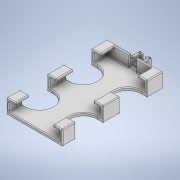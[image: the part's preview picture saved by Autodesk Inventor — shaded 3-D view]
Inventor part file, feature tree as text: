
AUTODESK INVENTOR PART (.ipt)
format: ipt  version: 2020.2 (Build 242310000, 310)  size: 641,536 bytes
history: native  units: in
note: dims shown in document units (in); Inventor stores cm internally (conversion verified against a paired STEP export)
features: sketch x7, extrude x6, fillet x5, hole x1
ambient origin geometry x8: Origin, YZ Plane, XZ Plane, XY Plane, X Axis, Y Axis, Z Axis, Center Point
bodies: Solid1 (feature_tree)
feature tree (19):
  extrude  "Extrusion1"  Depth=0.8in
  extrude  "Extrusion2"  Depth=0.5in
  extrude  "Extrusion3"  Depth=0.5in
  extrude  "Extrusion4"  Depth=0.8in
  hole  "Hole1"  [1 undecoded]
  sketch  "Sketch9"  dims[d12=0.15in d13=0.15in]
  extrude  "Extrusion5"  Depth=0.15in
  extrude  "Extrusion6"  Depth=0.3in
  fillet  "Fillet1"  Radius=0.3in
  fillet  "Fillet2"  Radius=0.3in
  fillet  "Fillet3"  Radius=0.3in
  fillet  "Fillet4"  Radius=0.15in
  fillet  "Fillet5"  Radius=0.15in
  sketch  "Sketch1"  dims[d0=3.3in d1=0.8in]
  sketch  "Sketch2"  dims[d2=5.8in d5=0.5in]
  sketch  "Sketch3"  dims[d6=1.0in d7=0.5in]
  sketch  "Sketch5"  dims[d8=1.0in d9=0.8in]
  sketch  "Sketch6"  dims[d10=0.2in d11=0.4in]
  sketch  "Sketch10"  dims[d14=0.77in d15=0.3in d16=0.3in d17=0.3in d18=0.3in d19=0.15in d20=0.15in d21=0.2in d22=0.0in d23=0.15in d24=0.15in d25=0.15in d26=0.15in d27=0.15in d28=0.15in d29=0.15in d30=0.15in d31=0.15in d32=0.09in d33=0.15in d34=0.09in d35=0.68in d36=0.0in d37=0.15in d38=0.0in d39=0.09in d40=0.15in d41=0.09in d42=0.15in d43=0.25in d44=0.0in d45=0.12in d46=0.75in d47=0.375in d48=0.25in d49=0.5635in d50=0.4in d51=0.8108in d55=0.15in d56=0.15in d57=0.15in d58=0.15in d59=0.8in d60=0.15in d61=0.4in d62=0.0in d63=0.4in d64=0.0in d65=0.8in d66=0.05in d67=0.05in d68=0.125in d69=0.05in]
note: 1 required parameter value undecoded (feature->parameter linkage not recoverable at this tier; creation-order binding heuristic only, values carry confidence <= 0.55)
